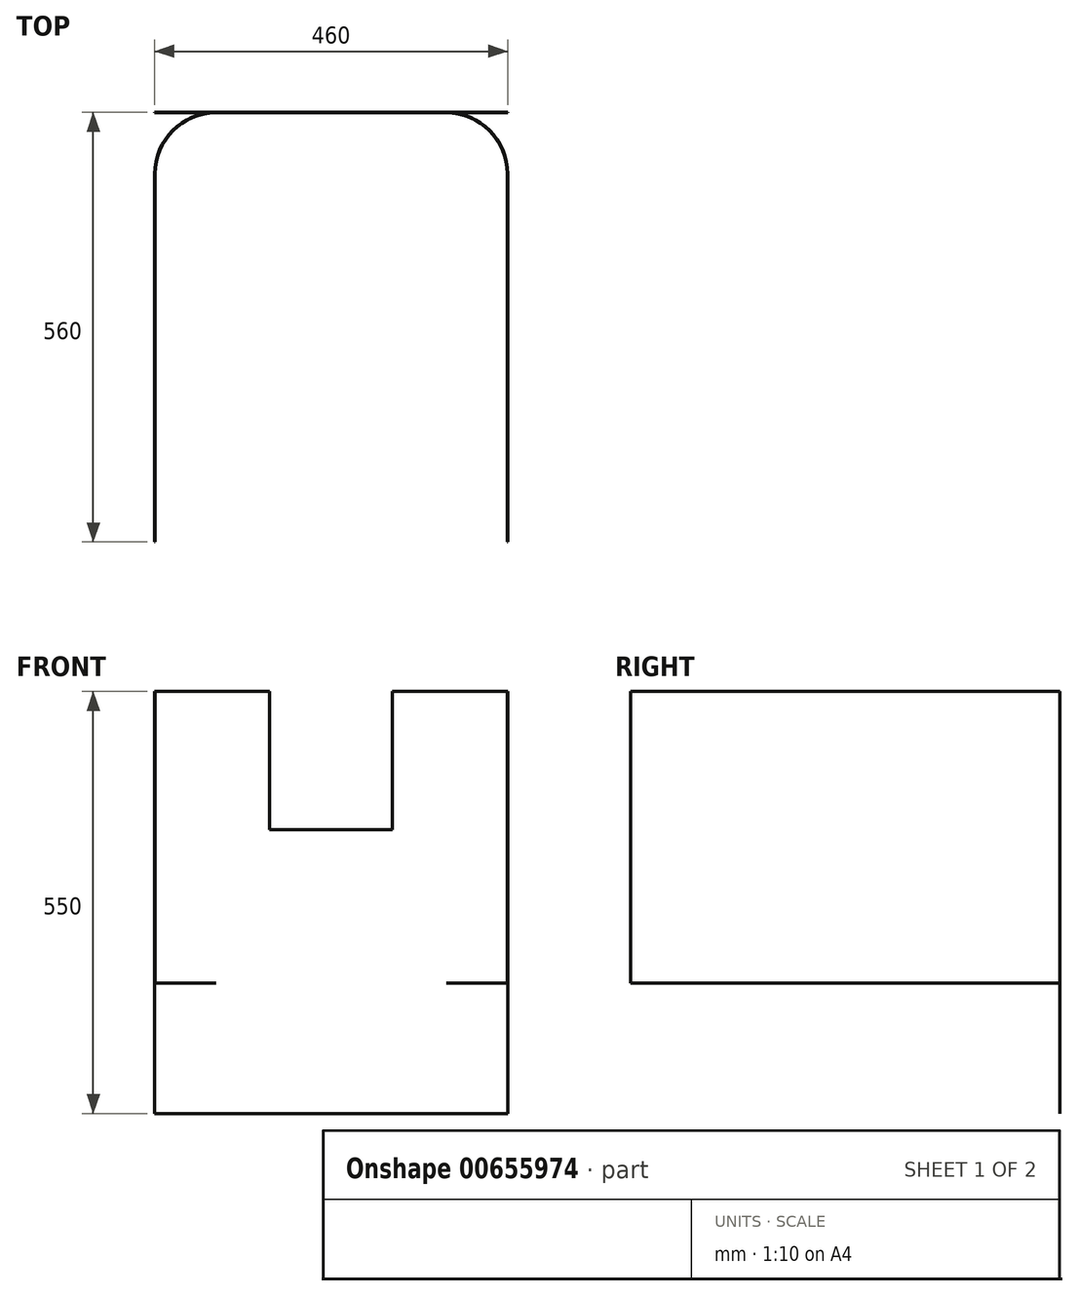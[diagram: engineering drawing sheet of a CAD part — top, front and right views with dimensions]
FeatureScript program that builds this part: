
annotation { "Feature Type Name" : "Feature", "Feature Type Description" : "" }
export const myFeature = defineFeature(function(context is Context, id is Id, definition is map)
    precondition{}
    {
        {
            var Q0;
            Q0=qCreatedBy(makeId("Top.planeOp"),FACE);
            var sketch = newSketch(context, id + "F0", { "sketchPlane" : qUnion([Q0])});
            skLineSegment(sketch, "E0", {"start": v(0, 0) * mm, "end": v(-150, 0) * mm});
            skLineSegment(sketch, "E1", {"start": v(-230, -80) * mm, "end": v(-230, -560) * mm});
            skPoint(sketch, "E2.visualSharp", {"position": v(-230, 0) * mm});
            skArc(sketch, "E2.filletArc", {"start": v(-150, 0) * mm, "mid": v(-206.57, -23.43) * mm, "end": v(-230, -80) * mm});
            skLineSegment(sketch, "E3.MirrorCS", {"start": v(0, 0) * mm, "end": v(150, 0) * mm});
            skArc(sketch, "E4.MirrorCS", {"start": v(150, 0) * mm, "mid": v(206.57, -23.43) * mm, "end": v(230, -80) * mm});
            skLineSegment(sketch, "E5.MirrorCS", {"start": v(230, -80) * mm, "end": v(230, -560) * mm});
            skLineSegment(sketch, "E6.0", {"start": v(-229.4, -80) * mm, "end": v(-229.4, -560) * mm});
            skArc(sketch, "E6.1", {"start": v(-150, -0.6) * mm, "mid": v(-206.14, -23.86) * mm, "end": v(-229.4, -80) * mm});
            skLineSegment(sketch, "E6.2", {"start": v(229.4, -80) * mm, "end": v(229.4, -560) * mm});
            skArc(sketch, "E6.3", {"start": v(150, -0.6) * mm, "mid": v(206.14, -23.86) * mm, "end": v(229.4, -80) * mm});
            skLineSegment(sketch, "E6.4", {"start": v(0, -0.6) * mm, "end": v(150, -0.6) * mm});
            skLineSegment(sketch, "E6.5", {"start": v(0, -0.6) * mm, "end": v(-150, -0.6) * mm});
            skLineSegment(sketch, "E7", {"start": v(-230, -560) * mm, "end": v(-229.4, -560) * mm});
            skLineSegment(sketch, "E8", {"start": v(229.4, -560) * mm, "end": v(230, -560) * mm});
            skSolve(sketch);
        }
        {
            var Q0;
            Q0=makeQuery(id+"F0.imprint","IMPRINT",FACE,{"disambiguationData":[TD([[makeQuery(id+"F0.imprint","IMPRINT",EDGE,{"derivedFrom":sQuery(id+"F0.wireOp",EDGE,"E0")}),1.0]])]});
            extrude(context, id + "F1", {"entities" : qUnion([Q0]), "depth" : 380 * mm, "offsetDistance" : 25.4 * mm});
        }
        {
            var Q0;
            Q0=makeQuery(id+"F1.opExtrude","SWEPT_FACE",FACE,{"disambiguationData":[OSD([sQuery(id+"F0.wireOp",EDGE,"E6.4"),sQuery(id+"F0.wireOp",EDGE,"E6.5")])]});
            var sketch = newSketch(context, id + "F2", { "sketchPlane" : qUnion([Q0])});
            skLineSegment(sketch, "E9.bottom", {"start": v(-80, 495.65) * mm, "end": v(0, 495.65) * mm});
            skLineSegment(sketch, "E9.top", {"start": v(-80, 200) * mm, "end": v(0, 200) * mm});
            skLineSegment(sketch, "E9.left", {"start": v(-80, 495.65) * mm, "end": v(-80, 200) * mm});
            skLineSegment(sketch, "E9.right", {"start": v(0, 495.65) * mm, "end": v(0, 200) * mm});
            skLineSegment(sketch, "E10.MirrorCS", {"start": v(80, 495.65) * mm, "end": v(80, 200) * mm});
            skLineSegment(sketch, "E11.MirrorCS", {"start": v(80, 200) * mm, "end": v(0, 200) * mm});
            skLineSegment(sketch, "E12.MirrorCS", {"start": v(80, 495.65) * mm, "end": v(0, 495.65) * mm});
            skSolve(sketch);
        }
        {
            var Q0;
            {var subQ0=sQuery(id+"F2.wireOp",EDGE,"E9.top");Q0=makeQuery(id+"F2.imprint","IMPRINT",FACE,{"disambiguationData":[TD([[makeQuery(id+"F2.imprint","IMPRINT",EDGE,{"derivedFrom":subQ0}),1.0]])]});}
            var Q1;
            {var subQ0=sQuery(id+"F2.wireOp",EDGE,"E11.MirrorCS");Q1=makeQuery(id+"F2.imprint","IMPRINT",FACE,{"disambiguationData":[TD([[makeQuery(id+"F2.imprint","IMPRINT",EDGE,{"derivedFrom":subQ0}),-1.0]])]});}
            var Q2;
            {var subQ0=sQuery(id+"F2.wireOp",EDGE,"E12.MirrorCS");Q2=makeQuery(id+"F2.imprint","IMPRINT",FACE,{"disambiguationData":[TD([[makeQuery(id+"F2.imprint","IMPRINT",EDGE,{"derivedFrom":subQ0}),1.0]])]});}
            var Q3;
            {var subQ0=sQuery(id+"F2.wireOp",EDGE,"E9.bottom");Q3=makeQuery(id+"F2.imprint","IMPRINT",FACE,{"disambiguationData":[TD([[makeQuery(id+"F2.imprint","IMPRINT",EDGE,{"derivedFrom":subQ0}),-1.0]])]});}
            extrude(context, id + "F3", {"entities" : qUnion([Q0, Q1, Q2, Q3]), "operationType" : NewBodyOperationType.REMOVE, "oppositeDirection" : true, "depth" : 25.4 * mm, "offsetDistance" : 25.4 * mm});
        }
        {
            var Q0;
            Q0=qCreatedBy(makeId("Front.planeOp"),FACE);
            var sketch = newSketch(context, id + "F4", { "sketchPlane" : qUnion([Q0])});
            skLineSegment(sketch, "E13.bottom", {"start": v(0, 0) * mm, "end": v(-230, 0) * mm});
            skLineSegment(sketch, "E13.top", {"start": v(0, -170) * mm, "end": v(-230, -170) * mm});
            skLineSegment(sketch, "E13.left", {"start": v(0, 0) * mm, "end": v(0, -170) * mm});
            skLineSegment(sketch, "E13.right", {"start": v(-230, 0) * mm, "end": v(-230, -170) * mm});
            skLineSegment(sketch, "E14.MirrorCS", {"start": v(0, -170) * mm, "end": v(230, -170) * mm});
            skLineSegment(sketch, "E15.MirrorCS", {"start": v(230, 0) * mm, "end": v(230, -170) * mm});
            skLineSegment(sketch, "E16.MirrorCS", {"start": v(0, 0) * mm, "end": v(230, 0) * mm});
            skSolve(sketch);
        }
        {
            var Q0;
            Q0=makeQuery(id+"F4.imprint","IMPRINT",FACE,{"disambiguationData":[TD([[makeQuery(id+"F4.imprint","IMPRINT",EDGE,{"derivedFrom":sQuery(id+"F4.wireOp",EDGE,"E13.left")}),1.0]])]});
            var Q1;
            Q1=makeQuery(id+"F4.imprint","IMPRINT",FACE,{"disambiguationData":[TD([[makeQuery(id+"F4.imprint","IMPRINT",EDGE,{"derivedFrom":sQuery(id+"F4.wireOp",EDGE,"E13.bottom")}),1.0]])]});
            extrude(context, id + "F5", {"entities" : qUnion([Q0, Q1]), "operationType" : NewBodyOperationType.ADD, "depth" : 0.6 * mm, "offsetDistance" : 25.4 * mm});
        }
    });
